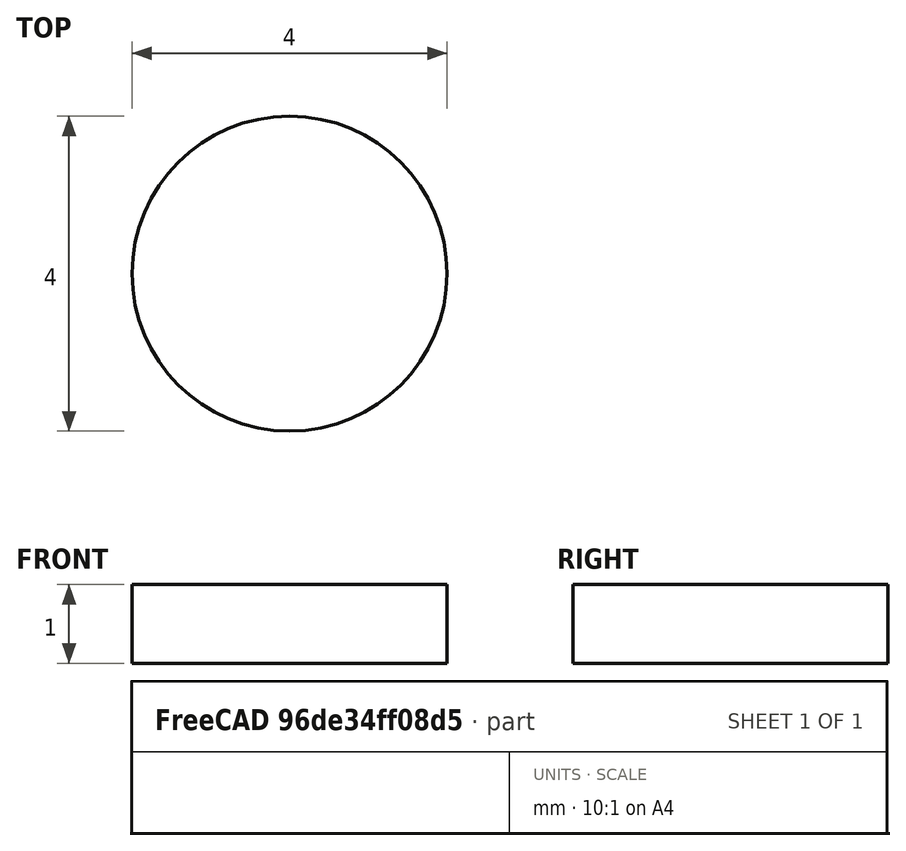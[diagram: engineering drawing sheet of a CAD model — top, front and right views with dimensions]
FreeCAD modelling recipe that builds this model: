
FCSTD DOCUMENT  (FreeCAD 0.21R33668 +26 (Git))
Label: Magnet_SPH
License: All rights reserved
LicenseURL: http://en.wikipedia.org/wiki/All_rights_reserved
objects: Sketcher::SketchObject×2, PartDesign::Pad×1, PartDesign::Body×1
note: 5 computed .brp shape members not serialized (recipe doc carries the construction recipe); baked Part::Feature solids carry a one-line shape summary decoded from their .brp

FEATURE [Sketcher::SketchObject] Sketch
  FullyConstrained = true
  MapMode = 5
  Support = -> [XY_Plane]
  sketch-geometry (1):
    g0: Circle CenterX=0 CenterY=0 CenterZ=0 NormalX=0 NormalY=0 NormalZ=1 AngleXU=0 Radius=2
  constraints (2):
    c: Coincident(g0,g-1)
    c: Diameter(g0) = 4  'Diameter'
FEATURE [PartDesign::Pad] Pad
  Direction = (0,0,1)
  Length = 1
  Length2 = 10
  Profile = -> Sketch
  ReferenceAxis = -> Sketch [N_Axis]
  Type = 0
FEATURE [Sketcher::SketchObject] Sketch001
  ExternalGeometry = -> [Pad]
  FullyConstrained = true
  MapMode = 5
  Placement = pos=(0,0,0) rot=(1,0,0;1.5708rad)
  Support = -> [XZ_Plane]
  constraints (1):
    c: DistanceY(g-4,g-3) = 1  'Height'
FEATURE [PartDesign::Body] Body  label="4x1mm"
  Group = -> [Sketch,Pad,Sketch001]
  Origin = -> Origin
  Tip = -> Pad
